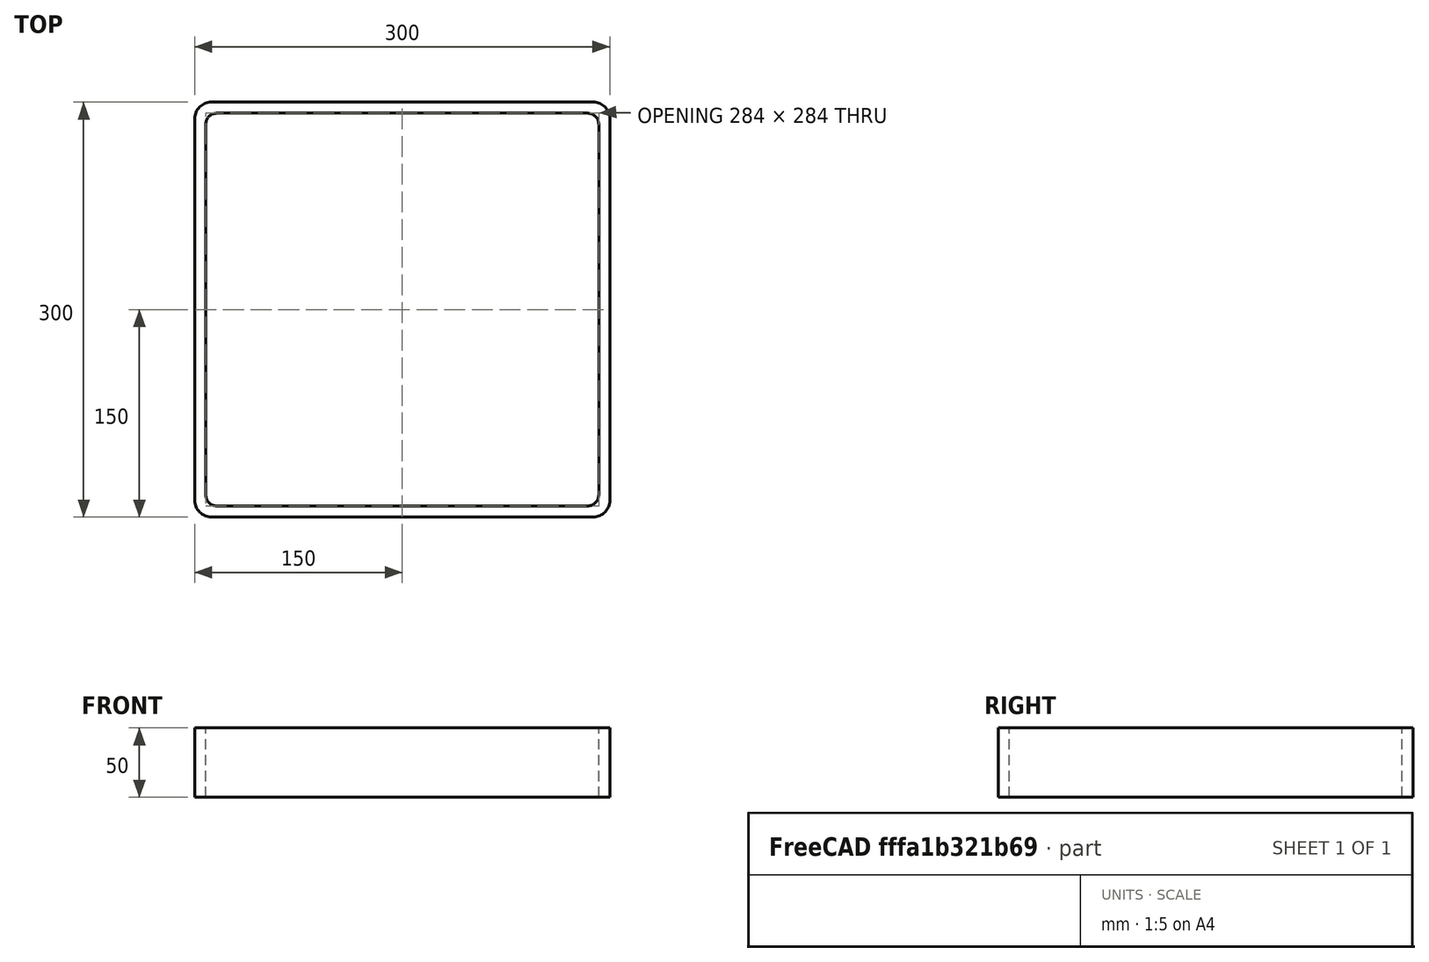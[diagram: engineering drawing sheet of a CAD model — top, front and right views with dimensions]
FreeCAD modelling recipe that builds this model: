
FCSTD DOCUMENT  (FreeCAD 0.15R4671 (Git))
Label: Square hollow section 300x300x8 EN10219 S235JRH
License: All rights reserved
LicenseURL: http://en.wikipedia.org/wiki/All_rights_reserved
objects: Sketcher::SketchObject×1, Part::Extrusion×1
note: 2 computed .brp shape members not serialized (recipe doc carries the construction recipe); baked Part::Feature solids carry a one-line shape summary decoded from their .brp

FEATURE [Sketcher::SketchObject] Sketch
  sketch-geometry (16):
    g0: LineSegment StartX=-134 StartY=142 StartZ=0 EndX=134 EndY=142 EndZ=0
    g1: LineSegment StartX=142 StartY=134 StartZ=0 EndX=142 EndY=-134 EndZ=0
    g2: LineSegment StartX=134 StartY=-142 StartZ=0 EndX=-134 EndY=-142 EndZ=0
    g3: LineSegment StartX=-142 StartY=-134 StartZ=0 EndX=-142 EndY=134 EndZ=0
    g4: LineSegment StartX=-138 StartY=150 StartZ=0 EndX=138 EndY=150 EndZ=0
    g5: LineSegment StartX=150 StartY=138 StartZ=0 EndX=150 EndY=-138 EndZ=0
    g6: LineSegment StartX=138 StartY=-150 StartZ=0 EndX=-138 EndY=-150 EndZ=0
    g7: LineSegment StartX=-150 StartY=-138 StartZ=0 EndX=-150 EndY=138 EndZ=0
    g8: ArcOfCircle CenterX=-134 CenterY=134 CenterZ=0 NormalX=0 NormalY=0 NormalZ=1 Radius=8 StartAngle=1.5708 EndAngle=3.14159
    g9: ArcOfCircle CenterX=134 CenterY=134 CenterZ=0 NormalX=0 NormalY=0 NormalZ=1 Radius=8 StartAngle=0 EndAngle=1.5708
    g10: ArcOfCircle CenterX=134 CenterY=-134 CenterZ=0 NormalX=0 NormalY=0 NormalZ=1 Radius=8 StartAngle=4.71239 EndAngle=6.28319
    g11: ArcOfCircle CenterX=-134 CenterY=-134 CenterZ=0 NormalX=0 NormalY=0 NormalZ=1 Radius=8 StartAngle=3.14159 EndAngle=4.71239
    g12: ArcOfCircle CenterX=138 CenterY=138 CenterZ=0 NormalX=0 NormalY=0 NormalZ=1 Radius=12 StartAngle=0 EndAngle=1.5708
    g13: ArcOfCircle CenterX=138 CenterY=-138 CenterZ=0 NormalX=0 NormalY=0 NormalZ=1 Radius=12 StartAngle=4.71239 EndAngle=6.28319
    g14: ArcOfCircle CenterX=-138 CenterY=-138 CenterZ=0 NormalX=0 NormalY=0 NormalZ=1 Radius=12 StartAngle=3.14159 EndAngle=4.71239
    g15: ArcOfCircle CenterX=-138 CenterY=138 CenterZ=0 NormalX=0 NormalY=0 NormalZ=1 Radius=12 StartAngle=1.5708 EndAngle=3.14159
  constraints (36):
    c: Horizontal(g2)
    c: Vertical(g3)
    c: Horizontal(g6)
    c: Vertical(g7)
    c: Tangent(g3,g8) = 1.5708
    c: Tangent(g0,g8) = 1.5708
    c: Tangent(g0,g9) = 1.5708
    c: Tangent(g1,g9) = 1.5708
    c: Tangent(g1,g10) = 1.5708
    c: Tangent(g2,g10) = 1.5708
    c: Tangent(g2,g11) = 1.5708
    c: Tangent(g3,g11) = 1.5708
    c: Tangent(g4,g12) = 1.5708
    c: Tangent(g5,g12) = 1.5708
    c: Tangent(g5,g13) = 1.5708
    c: Tangent(g6,g13) = 1.5708
    c: Tangent(g6,g14) = 1.5708
    c: Tangent(g7,g14) = 1.5708
    c: Tangent(g7,g15) = 1.5708
    c: Tangent(g4,g15) = 1.5708
    c: Equal(g9,g8)
    c: Equal(g9,g11)
    c: Equal(g9,g10)
    c: Equal(g12,g15)
    c: Equal(g12,g14)
    c: Equal(g12,g13)
    c: Symmetric(g4,g6,g-1)
    c: Symmetric(g7,g5,g-2)
    c: DistanceY(g4,g6) = -300
    c: DistanceX(g7,g5) = 300
    c: Symmetric(g3,g1,g-2)
    c: Symmetric(g0,g2,g-1)
    c: DistanceY(g0,g4) = 8
    c: DistanceX(g5,g1) = -8
    c: Radius(g9) = 8
    c: Radius(g12) = 12
FEATURE [Part::Extrusion] Extrude  label="Square hollow section 300x300x8 EN10219 S235JRH"
  Base = -> Sketch
  Dir = (0,0,50)
  Solid = true
